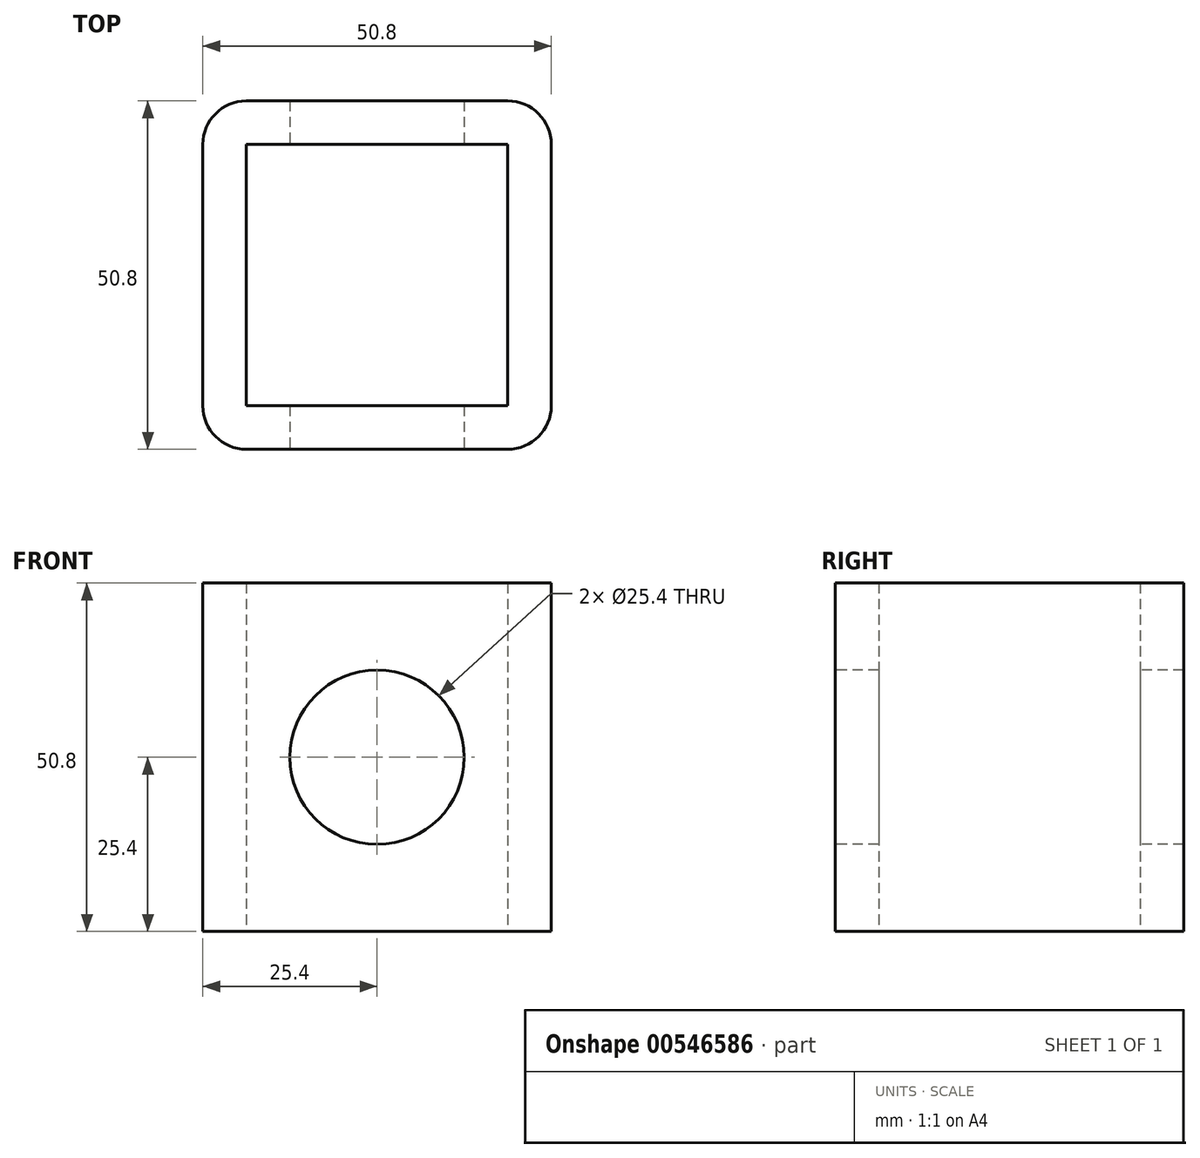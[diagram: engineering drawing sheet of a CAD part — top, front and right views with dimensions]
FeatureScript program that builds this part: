
annotation { "Feature Type Name" : "Feature", "Feature Type Description" : "" }
export const myFeature = defineFeature(function(context is Context, id is Id, definition is map)
    precondition{}
    {
        {
            var Q0;
            Q0=qCreatedBy(makeId("Top.planeOp"),FACE);
            var sketch = newSketch(context, id + "F0", { "sketchPlane" : qUnion([Q0])});
            skLineSegment(sketch, "E0.bottom", {"start": v(6.35, 0) * mm, "end": v(44.45, 0) * mm});
            skLineSegment(sketch, "E0.top", {"start": v(6.35, 50.8) * mm, "end": v(44.45, 50.8) * mm});
            skLineSegment(sketch, "E0.left", {"start": v(0, 6.35) * mm, "end": v(0, 44.45) * mm});
            skLineSegment(sketch, "E0.right", {"start": v(50.8, 6.35) * mm, "end": v(50.8, 44.45) * mm});
            skPoint(sketch, "E1.visualSharp", {"position": v(0, 50.8) * mm});
            skArc(sketch, "E1.filletArc", {"start": v(6.35, 50.8) * mm, "mid": v(1.86, 48.94) * mm, "end": v(0, 44.45) * mm});
            skPoint(sketch, "E2.visualSharp", {"position": v(0, 0) * mm});
            skArc(sketch, "E2.filletArc", {"start": v(0, 6.35) * mm, "mid": v(1.86, 1.86) * mm, "end": v(6.35, 0) * mm});
            skPoint(sketch, "E3.visualSharp", {"position": v(50.8, 0) * mm});
            skArc(sketch, "E3.filletArc", {"start": v(44.45, 0) * mm, "mid": v(48.94, 1.86) * mm, "end": v(50.8, 6.35) * mm});
            skPoint(sketch, "E4.visualSharp", {"position": v(50.8, 50.8) * mm});
            skArc(sketch, "E4.filletArc", {"start": v(50.8, 44.45) * mm, "mid": v(48.94, 48.94) * mm, "end": v(44.45, 50.8) * mm});
            skLineSegment(sketch, "E5.0", {"start": v(6.35, 6.35) * mm, "end": v(6.35, 44.45) * mm});
            skLineSegment(sketch, "E5.1", {"start": v(6.35, 6.35) * mm, "end": v(44.45, 6.35) * mm});
            skLineSegment(sketch, "E5.2", {"start": v(44.45, 6.35) * mm, "end": v(44.45, 44.45) * mm});
            skLineSegment(sketch, "E5.3", {"start": v(6.35, 44.45) * mm, "end": v(44.45, 44.45) * mm});
            skSolve(sketch);
        }
        {
            var Q0;
            Q0=makeQuery(id+"F0.imprint","IMPRINT",FACE,{"disambiguationData":[TD([[makeQuery(id+"F0.imprint","IMPRINT",EDGE,{"derivedFrom":sQuery(id+"F0.wireOp",EDGE,"E0.bottom")}),1.0]])]});
            extrude(context, id + "F1", {"entities" : qUnion([Q0]), "depth" : 50.8 * mm, "offsetDistance" : 25.4 * mm});
        }
        {
            var Q0;
            Q0=makeQuery(id+"F1.opExtrude","SWEPT_FACE",FACE,{"disambiguationData":[OSD([sQuery(id+"F0.wireOp",EDGE,"E0.bottom")])]});
            var sketch = newSketch(context, id + "F2", { "sketchPlane" : qUnion([Q0])});
            skCircle(sketch, "E6", {"center": v(25.4, 25.4) * mm, "radius": 12.7 * mm});
            skPoint(sketch, "E6.centerSnap0", {"position": v(44.45, 25.4) * mm});
            skPoint(sketch, "E6.centerSnap1", {"position": v(25.4, 50.8) * mm});
            skSolve(sketch);
        }
        {
            var Q0;
            Q0 = qSketchRegion(id + "F2", true);
            extrude(context, id + "F3", {"entities" : qUnion([Q0]), "operationType" : NewBodyOperationType.REMOVE, "endBound" : BoundingType.THROUGH_ALL, "oppositeDirection" : true, "depth" : 25.4 * mm, "offsetDistance" : 25.4 * mm});
        }
    });
